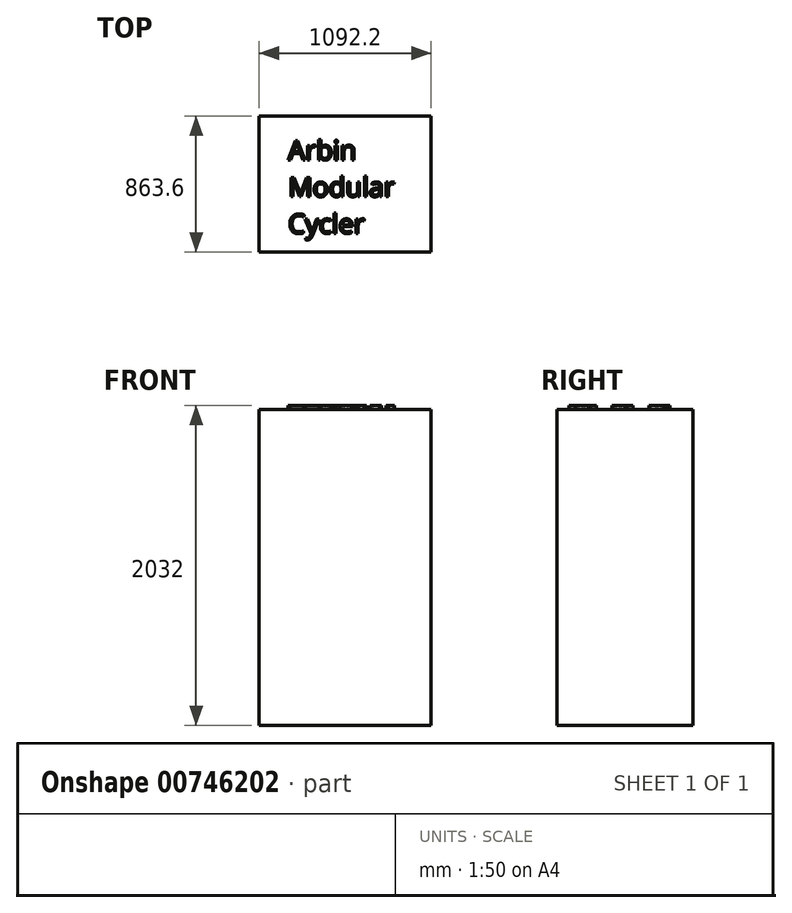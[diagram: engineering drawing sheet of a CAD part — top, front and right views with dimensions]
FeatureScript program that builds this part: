
annotation { "Feature Type Name" : "Feature", "Feature Type Description" : "" }
export const myFeature = defineFeature(function(context is Context, id is Id, definition is map)
    precondition{}
    {
        {
            var Q0;
            Q0=qCreatedBy(makeId("Top.planeOp"),FACE);
            var sketch = newSketch(context, id + "F0", { "sketchPlane" : qUnion([Q0])});
            skLineSegment(sketch, "E0.bottom", {"start": v(546.1, -431.8) * mm, "end": v(-546.1, -431.8) * mm});
            skLineSegment(sketch, "E0.top", {"start": v(546.1, 431.8) * mm, "end": v(-546.1, 431.8) * mm});
            skLineSegment(sketch, "E0.left", {"start": v(546.1, -431.8) * mm, "end": v(546.1, 431.8) * mm});
            skLineSegment(sketch, "E0.right", {"start": v(-546.1, -431.8) * mm, "end": v(-546.1, 431.8) * mm});
            skPoint(sketch, "E0.middle", {"position": v(0, 0) * mm});
            skSolve(sketch);
        }
        {
            var Q0;
            Q0=makeQuery(id+"F0.imprint","IMPRINT",FACE,{"disambiguationData":[TD([[makeQuery(id+"F0.imprint","IMPRINT",EDGE,{"derivedFrom":sQuery(id+"F0.wireOp",EDGE,"E0.bottom")}),-1.0]])]});
            extrude(context, id + "F1", {"entities" : qUnion([Q0]), "depth" : 2006.6 * mm, "offsetDistance" : 25.4 * mm});
        }
        {
            var Q0;
            Q0=makeQuery(id+"F1.opExtrude","CAP_FACE",FACE,{"disambiguationData":[OSD([sQuery(id+"F0.wireOp",EDGE,"E0.bottom"),sQuery(id+"F0.wireOp",EDGE,"E0.top"),sQuery(id+"F0.wireOp",EDGE,"E0.left"),sQuery(id+"F0.wireOp",EDGE,"E0.right")])],"isStart":false});
            var sketch = newSketch(context, id + "F2", { "sketchPlane" : qUnion([Q0])});
            skText(sketch, "E1", { "text": "Arbin \nModular\nCycler", "fontName": "OpenSans-Regular.ttf"});
            const initialGuessF2  = {"E1": [-0.36207, 0.15325, 1, 0, 0.12362]};
            skSetInitialGuess(sketch, initialGuessF2);
            skSolve(sketch);
        }
        {
            var Q0;
            Q0 = qSketchRegion(id + "F2", true);
            extrude(context, id + "F3", {"entities" : qUnion([Q0]), "operationType" : NewBodyOperationType.ADD, "depth" : 25.4 * mm, "offsetDistance" : 25.4 * mm});
        }
    });
